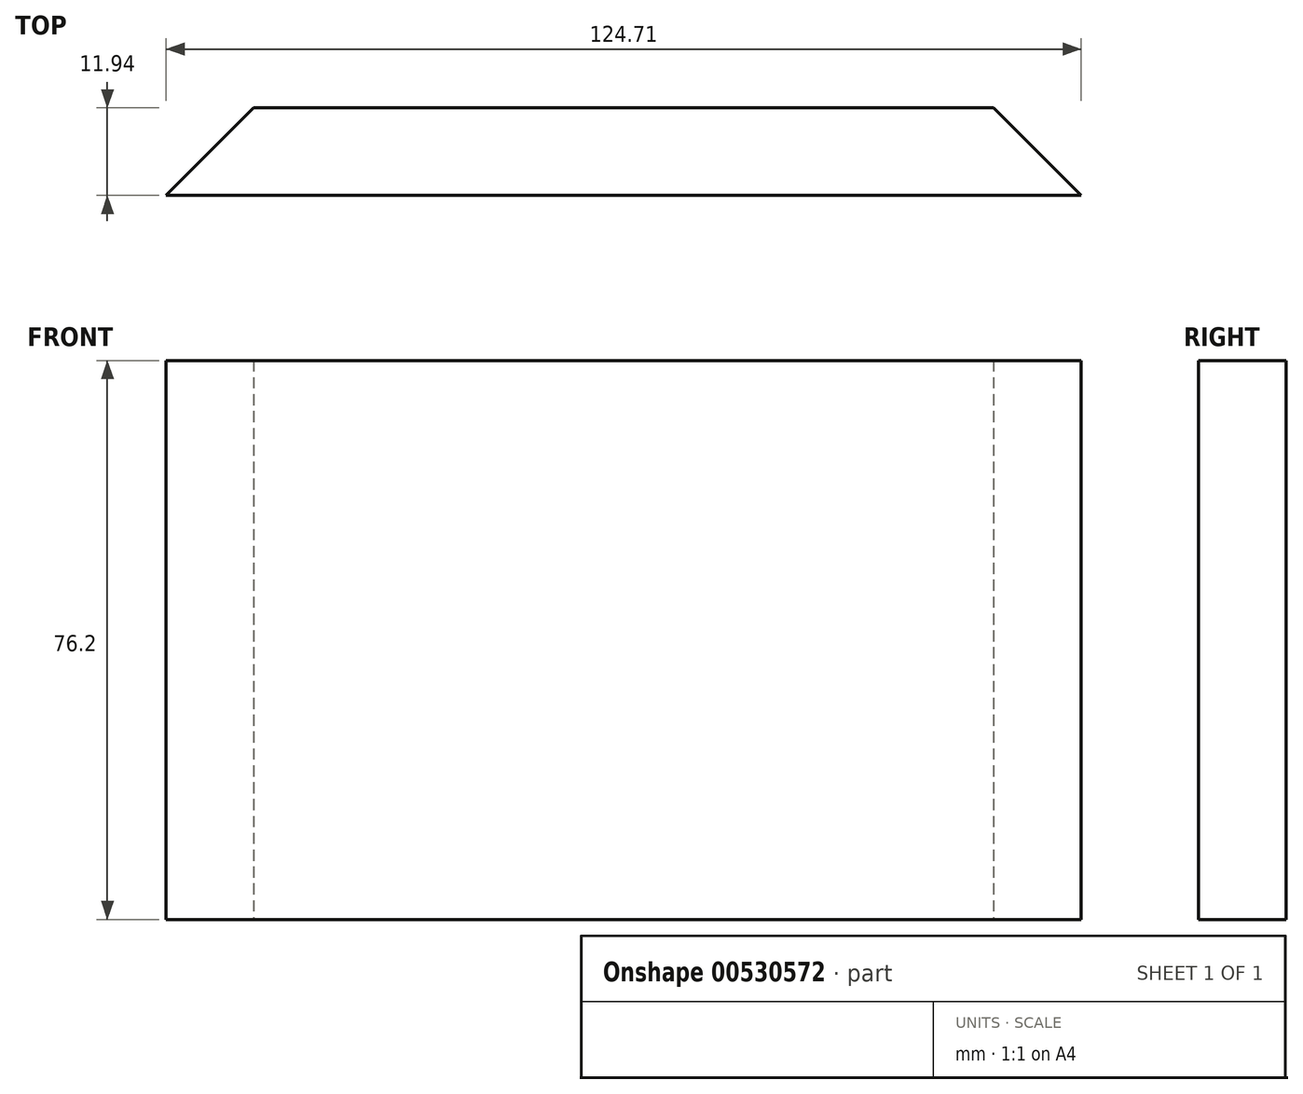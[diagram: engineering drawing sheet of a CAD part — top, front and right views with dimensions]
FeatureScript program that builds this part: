
annotation { "Feature Type Name" : "Feature", "Feature Type Description" : "" }
export const myFeature = defineFeature(function(context is Context, id is Id, definition is map)
    precondition{}
    {
        {
            var Q0;
            Q0=qCreatedBy(makeId("Front.planeOp"),FACE);
            var sketch = newSketch(context, id + "F0", { "sketchPlane" : qUnion([Q0])});
            skLineSegment(sketch, "E0.bottom", {"start": v(0, 0) * mm, "end": v(124.71, 0) * mm});
            skLineSegment(sketch, "E0.top", {"start": v(0, -76.2) * mm, "end": v(124.71, -76.2) * mm});
            skLineSegment(sketch, "E0.left", {"start": v(0, 0) * mm, "end": v(0, -76.2) * mm});
            skLineSegment(sketch, "E0.right", {"start": v(124.71, 0) * mm, "end": v(124.71, -76.2) * mm});
            skSolve(sketch);
        }
        {
            var Q0;
            Q0 = qSketchRegion(id + "F0", true);
            extrude(context, id + "F1", {"entities" : qUnion([Q0]), "depth" : 11.94 * mm, "offsetDistance" : 25.4 * mm});
        }
        {
            var Q0;
            Q0=makeQuery(id+"F1.opExtrude","SWEPT_FACE",FACE,{"disambiguationData":[OSD([sQuery(id+"F0.wireOp",EDGE,"E0.top")])]});
            var sketch = newSketch(context, id + "F2", { "sketchPlane" : qUnion([Q0])});
            skLineSegment(sketch, "E1", {"start": v(0, 11.94) * mm, "end": v(11.94, 0) * mm});
            skLineSegment(sketch, "E2", {"start": v(0, 11.94) * mm, "end": v(0, 0) * mm});
            skLineSegment(sketch, "E3", {"start": v(0, 0) * mm, "end": v(11.94, 0) * mm});
            skSolve(sketch);
        }
        {
            var Q0;
            Q0 = qSketchRegion(id + "F2", true);
            extrude(context, id + "F3", {"entities" : qUnion([Q0]), "operationType" : NewBodyOperationType.REMOVE, "endBound" : BoundingType.THROUGH_ALL, "oppositeDirection" : true, "depth" : 25.4 * mm, "offsetDistance" : 25.4 * mm});
        }
        {
            var Q0;
            Q0=makeQuery(id+"F1.opExtrude","SWEPT_FACE",FACE,{"disambiguationData":[OSD([sQuery(id+"F0.wireOp",EDGE,"E0.top")])]});
            var sketch = newSketch(context, id + "F4", { "sketchPlane" : qUnion([Q0])});
            skLineSegment(sketch, "E4", {"start": v(124.71, 11.94) * mm, "end": v(112.78, 0) * mm});
            skLineSegment(sketch, "E5", {"start": v(124.71, 11.94) * mm, "end": v(124.71, 0) * mm});
            skLineSegment(sketch, "E6", {"start": v(124.71, 0) * mm, "end": v(112.78, 0) * mm});
            skSolve(sketch);
        }
        {
            var Q0;
            Q0 = qSketchRegion(id + "F4", true);
            extrude(context, id + "F5", {"entities" : qUnion([Q0]), "operationType" : NewBodyOperationType.REMOVE, "endBound" : BoundingType.THROUGH_ALL, "oppositeDirection" : true, "depth" : 25.4 * mm, "offsetDistance" : 25.4 * mm});
        }
    });
